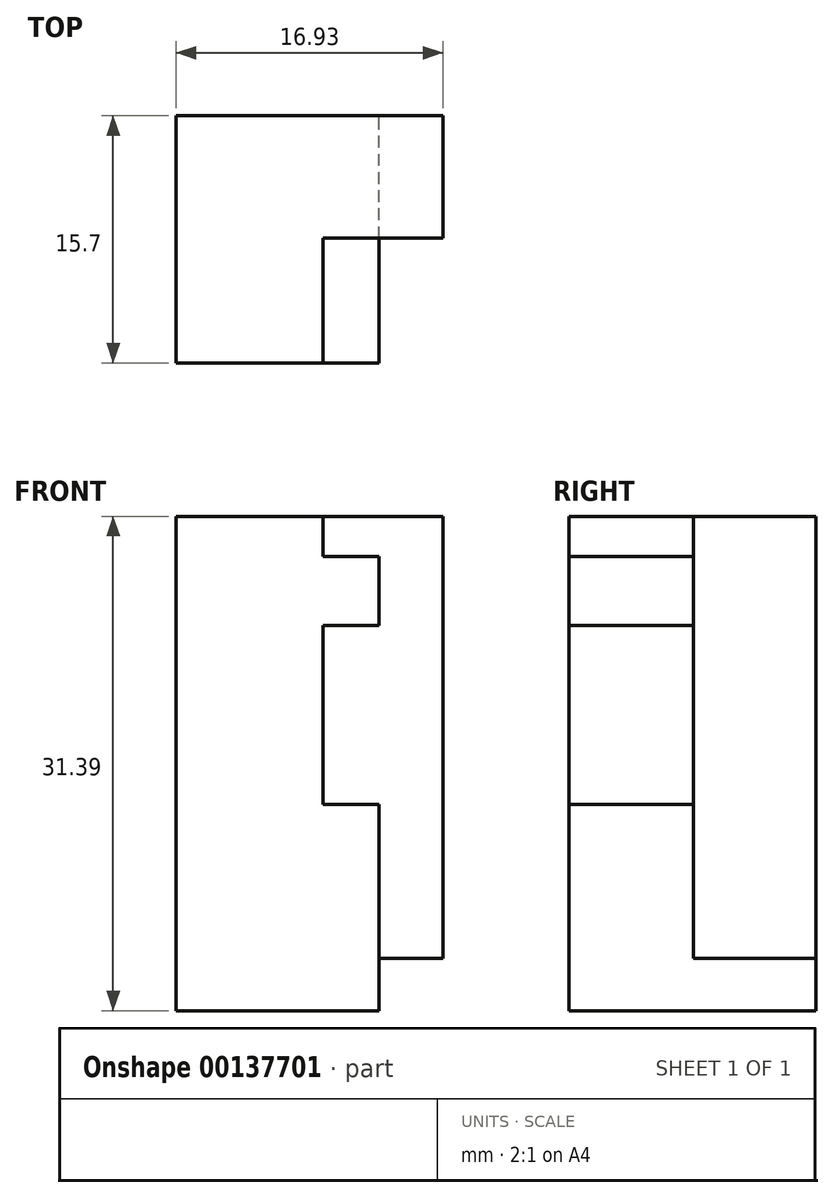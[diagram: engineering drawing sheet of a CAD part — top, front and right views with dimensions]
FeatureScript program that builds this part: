
annotation { "Feature Type Name" : "Feature", "Feature Type Description" : "" }
export const myFeature = defineFeature(function(context is Context, id is Id, definition is map)
    precondition{}
    {
        {
            var Q0;
            Q0=qCreatedBy(makeId("Front.planeOp"),FACE);
            var sketch = newSketch(context, id + "F0", { "sketchPlane" : qUnion([Q0])});
            skLineSegment(sketch, "E0.bottom", {"start": v(19.22, -39.26) * mm, "end": v(6.35, -39.26) * mm});
            skLineSegment(sketch, "E0.top", {"start": v(19.22, -26.17) * mm, "end": v(6.35, -26.17) * mm});
            skLineSegment(sketch, "E0.left", {"start": v(19.22, -39.26) * mm, "end": v(19.22, -26.17) * mm});
            skLineSegment(sketch, "E0.right", {"start": v(6.35, -39.26) * mm, "end": v(6.35, -26.17) * mm});
            skLineSegment(sketch, "E1.top", {"start": v(19.22, -35.93) * mm, "end": v(23.28, -35.93) * mm});
            skLineSegment(sketch, "E1.left", {"start": v(19.22, -39.26) * mm, "end": v(19.22, -35.93) * mm});
            skLineSegment(sketch, "E2", {"start": v(15.66, -26.17) * mm, "end": v(15.66, -14.8) * mm});
            skLineSegment(sketch, "E3", {"start": v(15.66, -14.8) * mm, "end": v(19.22, -14.8) * mm});
            skLineSegment(sketch, "E4", {"start": v(19.22, -14.8) * mm, "end": v(19.22, -10.43) * mm});
            skLineSegment(sketch, "E5", {"start": v(19.22, -10.43) * mm, "end": v(15.66, -10.43) * mm});
            skLineSegment(sketch, "E6", {"start": v(15.66, -10.43) * mm, "end": v(15.66, -7.87) * mm});
            skLineSegment(sketch, "E7", {"start": v(15.66, -7.87) * mm, "end": v(6.35, -7.87) * mm});
            skLineSegment(sketch, "E8", {"start": v(6.35, -7.87) * mm, "end": v(6.35, -26.17) * mm});
            skLineSegment(sketch, "E9", {"start": v(23.28, -35.93) * mm, "end": v(23.28, -7.87) * mm});
            skLineSegment(sketch, "E10", {"start": v(23.28, -7.87) * mm, "end": v(15.66, -7.87) * mm});
            skSolve(sketch);
        }
        {
            var Q0;
            Q0=makeQuery(id+"F0.imprint","IMPRINT",FACE,{"disambiguationData":[TD([[makeQuery(id+"F0.imprint","IMPRINT",EDGE,{"derivedFrom":sQuery(id+"F0.wireOp",EDGE,"E0.bottom")}),-1.0]])]});
            var Q1;
            {var subQ2=sQuery(id+"F0.wireOp",EDGE,"E2");Q1=makeQuery(id+"F0.imprint","IMPRINT",FACE,{"disambiguationData":[TD([[makeQuery(id+"F0.imprint","IMPRINT",EDGE,{"derivedFrom":subQ2}),1.0]])]});}
            extrude(context, id + "F1", {"entities" : qUnion([Q0, Q1]), "depth" : 15.7 * mm});
        }
        {
            var Q0;
            {var subQ1=sQuery(id+"F0.wireOp",EDGE,"E0.left");Q0=makeQuery(id+"F0.imprint","IMPRINT",FACE,{"disambiguationData":[TD([[makeQuery(id+"F0.imprint","IMPRINT",EDGE,{"derivedFrom":subQ1}),-1.0]])]});}
            extrude(context, id + "F2", {"entities" : qUnion([Q0]), "operationType" : NewBodyOperationType.ADD, "depth" : 7.77 * mm});
        }
    });
